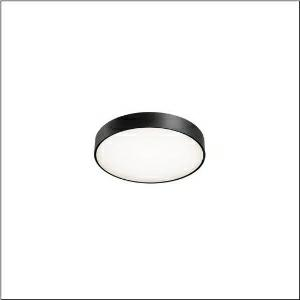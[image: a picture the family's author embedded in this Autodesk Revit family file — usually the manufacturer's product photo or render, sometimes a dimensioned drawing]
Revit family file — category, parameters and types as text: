
# Revit family: round_21_s_51mr34gd0421b
name_source: partatom
category: Lighting Fixtures
units: mm (PartAtom-declared; Revit-internal decimal feet)

## family parameters
Cut with Voids When Loaded = No
Host = Face
Light Source = No
Part Type = Normal
Room Calculation Point = No
Round Connector Dimension = Use Diameter
Shared = No

## types (1)
- Round 21 S (1 x LED, 4090 lm, 28.3 W, 4000K)
    Apparent Load = 28 VA
    CIE Flux Codes = 49 80 96 79 100
    Color Rendering = 80
    Color Temperature = 4000K
    Default Elevation = 1800 mm
    Description = Round 21 S, wall and ceiling luminaire, primary optical cover: cover, of PMMA, opal, light emission: direct/indirect distribution, primary light characteristic: symmetric, installation type: suspended mounting, surface-mounted, LED, rated luminous flux: 4.090lm, luminous efficacy: 135lm/W, light colour: 840, colour temperature: 4000K, control gear: DALI 2, with terminal, 5-pole, mains connection: 230V, AC, 50/60Hz, rated input power: 28.3W, housing, of aluminium, coated, black, diameter: 400mm, height: 62mm, protection rating (complete): IP40, insulation class (complete): insulation class I (protective earthing), certification: CE, impact resistance: IK04, permissible operating ambient temperature: -10..+35°C, packaging unit: 1 piece
    Height = 87 mm
    Lamp = 1 x LED
    Lamp Light Flux = 4090 lm
    Lamp Power = 28.3 W
    Lamp count = 1
    Length = 400 mm
    Luminous efficacy = 145 lm/W
    Manufacturer = Siteco
    ModVariant = No
    Model = 51MR34GD0421B
    Mounting Place = Ceiling
    Mounting Type = Surface mounted
    Number of Poles = 1
    OnlyDefault = Yes
    Power Factor = 1
    Product Name = Round 21 S
    Product group = wall and ceiling luminaire
    ProductGroupID = 304
    Protection Class = Protection class I
    Protection Degree = IP 40
    RLX_Detail_Level = 1
    RLX_Emergency_Light_Flux = 0 lm
    RLX_Emergency_Type = 0
    RLX_Emergency_Type_DB = No
    RlxData = <blob elided: 13873 chars, md5=0a4a3f46>
    Socket = socket
    Standby Power = 0 W
    System Light Flux = 4090 lm
    System Power = 28 W
    Type Comments = Product without accessories
    Type Image = l_1258311.jpg
    URL = http://relux.com
    VarID = ---
    Voltage = 0 V
    Weight = 0.00 kg
    Width = 0 mm  [stored 0 ft]

note: [stored X ft] marks values corroborated as IEEE doubles in the binary element streams (Revit-internal decimal feet)

## geometry (parser evidence)
native form markers: Sweep x15
no freeform markers — native parametric forms only
